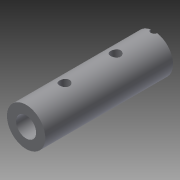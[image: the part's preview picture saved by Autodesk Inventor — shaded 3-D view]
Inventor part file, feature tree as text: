
AUTODESK INVENTOR PART (.ipt)
format: ipt  version: 2015 (Build 190159000, 159)  size: 126,464 bytes
history: native  units: in
note: dims shown in document units (in); Inventor stores cm internally (conversion verified against a paired STEP export)
features: sketch x1, revolve x1, extrude x1
ambient origin geometry x8: Origin, YZ Plane, XZ Plane, XY Plane, X Axis, Y Axis, Z Axis, Center Point
bodies: Solid1 (feature_tree)
feature tree (3):
  sketch  "Sketch1"  dims[d0=0.1181in d1=0.7874in d2=0.1181in d3=0.315in d4=0.122in d5=0.1181in d6=0.124in d7=0.7874in d8=0.315in d9=0.122in d10=90.0deg d11=0.0787in d12=0.7874in d13=0.0in]
  revolve  "Revolution1"  [1 undecoded]
  extrude  "Extrusion1"  Depth=0.7874in
note: 1 required parameter value undecoded (feature->parameter linkage not recoverable at this tier; creation-order binding heuristic only, values carry confidence <= 0.55)
